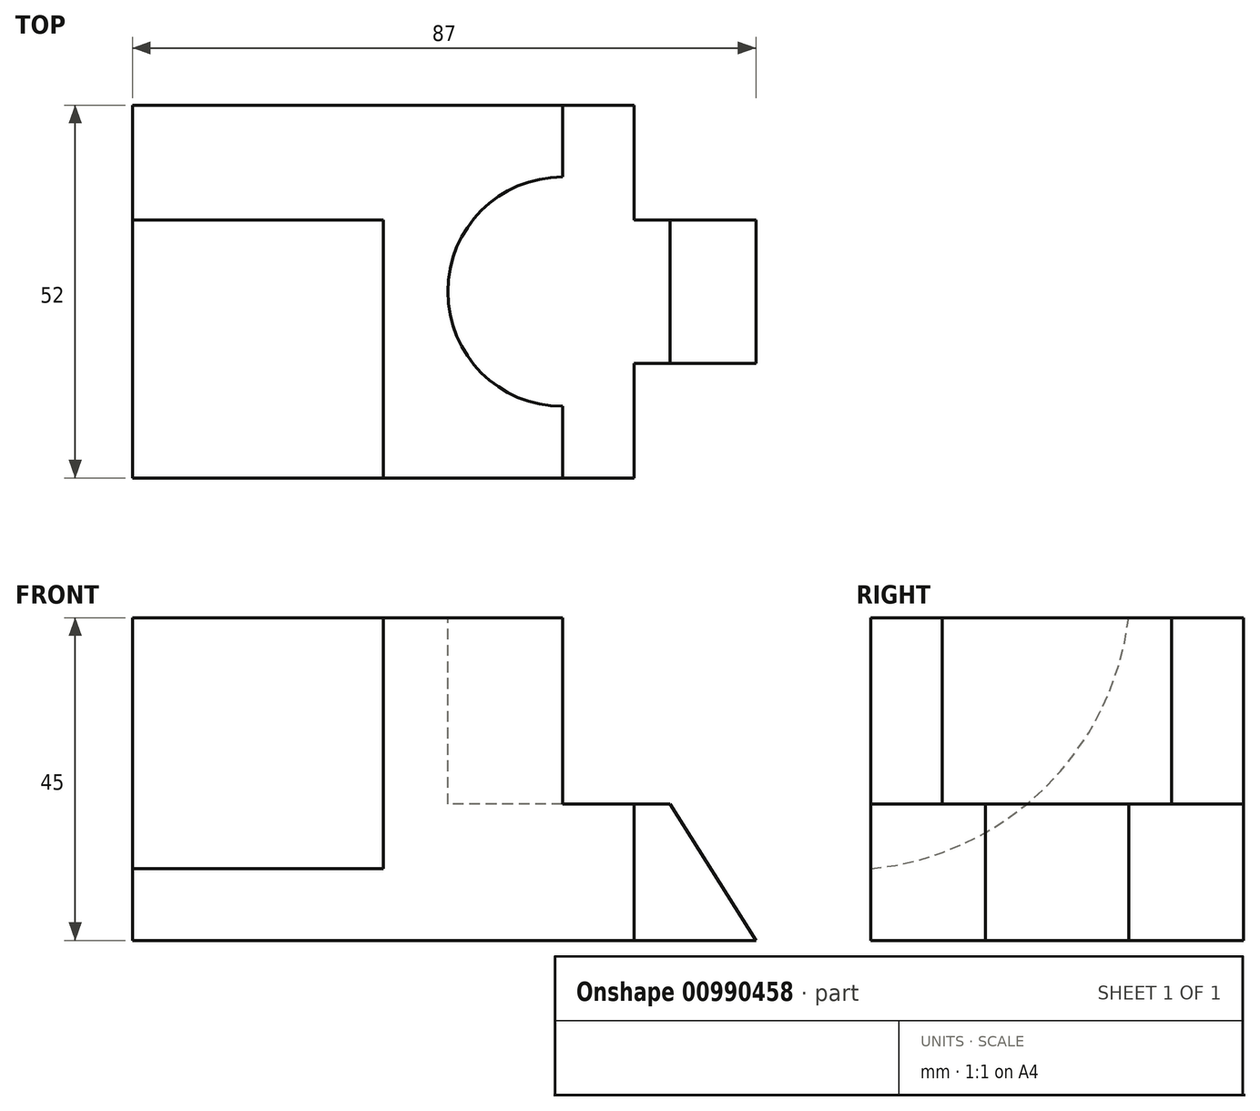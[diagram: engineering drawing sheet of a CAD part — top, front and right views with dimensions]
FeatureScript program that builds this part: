
annotation { "Feature Type Name" : "Feature", "Feature Type Description" : "" }
export const myFeature = defineFeature(function(context is Context, id is Id, definition is map)
    precondition{}
    {
        {
            var Q0;
            Q0=qCreatedBy(makeId("Top.planeOp"),FACE);
            cPlane(context, id + "F0", {"entities" : qUnion([Q0]), "cplaneType" : CPlaneType.OFFSET, "offset" : 19 * mm, "oppositeDirection" : true, "width" : 150 * mm, "height" : 150 * mm});
        }
        {
            var Q0;
            Q0=qCreatedBy(id+"F0.planeOp",FACE);
            var sketch = newSketch(context, id + "F1", { "sketchPlane" : qUnion([Q0])});
            skLineSegment(sketch, "E0.bottom", {"start": v(35, -26) * mm, "end": v(-35, -26) * mm});
            skLineSegment(sketch, "E0.top", {"start": v(35, 26) * mm, "end": v(-35, 26) * mm});
            skLineSegment(sketch, "E0.left", {"start": v(35, -26) * mm, "end": v(35, 26) * mm});
            skLineSegment(sketch, "E0.right", {"start": v(-35, -26) * mm, "end": v(-35, 26) * mm});
            skPoint(sketch, "E0.middle", {"position": v(0, 0) * mm});
            skSolve(sketch);
        }
        {
            var Q0;
            Q0 = qSketchRegion(id + "F1", true);
            extrude(context, id + "F2", {"entities" : qUnion([Q0]), "depth" : 45 * mm, "offsetDistance" : 25 * mm});
        }
        {
            var Q0;
            Q0=qCreatedBy(makeId("Top.planeOp"),FACE);
            cPlane(context, id + "F3", {"entities" : qUnion([Q0]), "cplaneType" : CPlaneType.OFFSET, "offset" : 26 * mm, "width" : 150 * mm, "height" : 150 * mm});
        }
        {
            var Q0;
            Q0=qCreatedBy(id+"F3.planeOp",FACE);
            var sketch = newSketch(context, id + "F4", { "sketchPlane" : qUnion([Q0])});
            skLineSegment(sketch, "E1", {"start": v(0, 0) * mm, "end": v(35, 0) * mm, "construction": true});
            skLineSegment(sketch, "E2.MirrorCS", {"start": v(0, 0) * mm, "end": v(-35, 0) * mm, "construction": true});
            skLineSegment(sketch, "E3", {"start": v(35, 0) * mm, "end": v(25, 0) * mm, "construction": true});
            skCircle(sketch, "E4", {"center": v(25, 0) * mm, "radius": 16 * mm});
            skLineSegment(sketch, "E5", {"start": v(25, 28.96) * mm, "end": v(25, -30.28) * mm});
            skLineSegment(sketch, "E6", {"start": v(25, -30.28) * mm, "end": v(53.92, -30.28) * mm});
            skLineSegment(sketch, "E7", {"start": v(53.92, -30.28) * mm, "end": v(53.92, 29.17) * mm});
            skLineSegment(sketch, "E8", {"start": v(53.92, 29.17) * mm, "end": v(25, 28.96) * mm});
            skSolve(sketch);
        }
        {
            var Q0;
            Q0 = qSketchRegion(id + "F4", true);
            extrude(context, id + "F5", {"entities" : qUnion([Q0]), "operationType" : NewBodyOperationType.REMOVE, "oppositeDirection" : true, "depth" : 26 * mm, "offsetDistance" : 25 * mm});
        }
        {
            var Q0;
            Q0=qCreatedBy(makeId("Right.planeOp"),FACE);
            var sketch = newSketch(context, id + "F6", { "sketchPlane" : qUnion([Q0])});
            skLineSegment(sketch, "E9", {"start": v(0, 0) * mm, "end": v(-26, 0) * mm, "construction": true});
            skLineSegment(sketch, "E10", {"start": v(-26, 0) * mm, "end": v(-26, -19) * mm, "construction": true});
            skLineSegment(sketch, "E11", {"start": v(-26, -19) * mm, "end": v(-26, -9) * mm, "construction": true});
            skLineSegment(sketch, "E12", {"start": v(-26, 0) * mm, "end": v(-26, 26) * mm, "construction": true});
            skLineSegment(sketch, "E13", {"start": v(-26, 26) * mm, "end": v(26, 26) * mm, "construction": true});
            skLineSegment(sketch, "E14", {"start": v(26, 26) * mm, "end": v(10, 26) * mm, "construction": true});
            skArc(sketch, "E15", {"start": v(10, 26) * mm, "mid": v(-1.82, 2.15) * mm, "end": v(-26, -9) * mm});
            skLineSegment(sketch, "E16", {"start": v(10, 26) * mm, "end": v(-26, 26) * mm});
            skLineSegment(sketch, "E17", {"start": v(-26, 26) * mm, "end": v(-26, -9) * mm});
            skSolve(sketch);
        }
        {
            var Q0;
            Q0 = qSketchRegion(id + "F6", true);
            extrude(context, id + "F7", {"entities" : qUnion([Q0]), "operationType" : NewBodyOperationType.REMOVE, "endBound" : BoundingType.UP_TO_NEXT, "oppositeDirection" : true, "depth" : 25 * mm, "offsetDistance" : 25 * mm});
        }
        {
            var Q0;
            Q0=qCreatedBy(makeId("Front.planeOp"),FACE);
            var sketch = newSketch(context, id + "F8", { "sketchPlane" : qUnion([Q0])});
            skLineSegment(sketch, "E18", {"start": v(0, 0) * mm, "end": v(0, -19) * mm, "construction": true});
            skLineSegment(sketch, "E19", {"start": v(0, -19) * mm, "end": v(52, -19) * mm});
            skLineSegment(sketch, "E20", {"start": v(0, 0) * mm, "end": v(40, 0) * mm});
            skLineSegment(sketch, "E21", {"start": v(40, 0) * mm, "end": v(52, -19) * mm});
            skLineSegment(sketch, "E22", {"start": v(0, 0) * mm, "end": v(0, -19) * mm});
            skSolve(sketch);
        }
        {
            var Q0;
            Q0 = qSketchRegion(id + "F8", true);
            extrude(context, id + "F9", {"entities" : qUnion([Q0]), "operationType" : NewBodyOperationType.ADD, "endBound" : BoundingType.SYMMETRIC, "depth" : 20 * mm, "offsetDistance" : 25 * mm});
        }
    });
